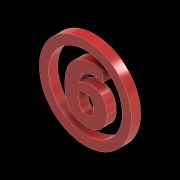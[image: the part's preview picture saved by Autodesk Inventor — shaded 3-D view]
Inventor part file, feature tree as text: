
AUTODESK INVENTOR PART (.ipt)
format: ipt  version: 2020 (Build 240168000, 168)  size: 178,688 bytes
history: native  units: mm
features: other x5, extrude x2, sketch x2
ambient origin geometry x8: Origin, YZ Plane, XZ Plane, XY Plane, X Axis, Y Axis, Z Axis, Center Point
bodies: Body1 (feature_tree)
feature tree (9):
  other  "自動販賣機.ipt"
  extrude  "擠出1"  Depth=10.0mm
  extrude  "擠出2"  Depth=10.0mm TaperAngle=0.0deg
  other  "實體49::自動販賣機.ipt"
  other  "標籤特徵1"
  sketch  "草圖1"
  sketch  "草圖2"
  other  "實體1"
  other  "投影切割邊1"
